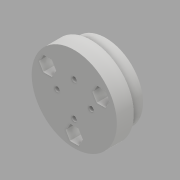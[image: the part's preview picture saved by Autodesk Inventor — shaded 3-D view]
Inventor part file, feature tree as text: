
AUTODESK INVENTOR PART (.ipt)
format: ipt  version: 2017 (Build 210142000, 142)  size: 162,816 bytes
history: native  units: mm
features: sketch x5, extrude x3, hole x2
ambient origin geometry x8: Origin, YZ Plane, XZ Plane, XY Plane, X Axis, Y Axis, Z Axis, Center Point
bodies: Solid1 (feature_tree)
feature tree (10):
  extrude  "Extrusion1"  Depth=2.0mm
  extrude  "Extrusion2"  Depth=2.0mm
  hole  "Hole1"  [1 undecoded]
  hole  "Hole2"  [1 undecoded]
  extrude  "Extrusion3"  Depth=6.0mm
  sketch  "Sketch1"  dims[d0=16.0mm d1=2.0mm]
  sketch  "Sketch2"  dims[d2=2.0mm d3=2.0mm]
  sketch  "Sketch3"  dims[d4=2.0mm d5=4.0mm]
  sketch  "Sketch4"  dims[d6=30.0mm d8=360.0deg d10=13.0mm]
  sketch  "Sketch5"  dims[d11=90.0deg d12=40.0mm d13=8.0mm d14=0.0mm d15=35.0mm d16=6.8mm d17=0.0mm d20=2.3mm d21=6.0mm d22=5.5mm d23=6.0mm d24=90.0deg d25=8.0mm d26=20.594885mm d27=29.0mm d28=30.0mm d30=360.0deg d32=4.3mm d33=6.0mm d34=7.0mm d35=6.0mm d36=90.0deg d37=8.0mm d38=20.594885mm d39=7.0mm d40=30.0mm d42=360.0deg d44=6.0mm d45=0.0mm]
note: 2 required parameter values undecoded (feature->parameter linkage not recoverable at this tier; creation-order binding heuristic only, values carry confidence <= 0.55)
